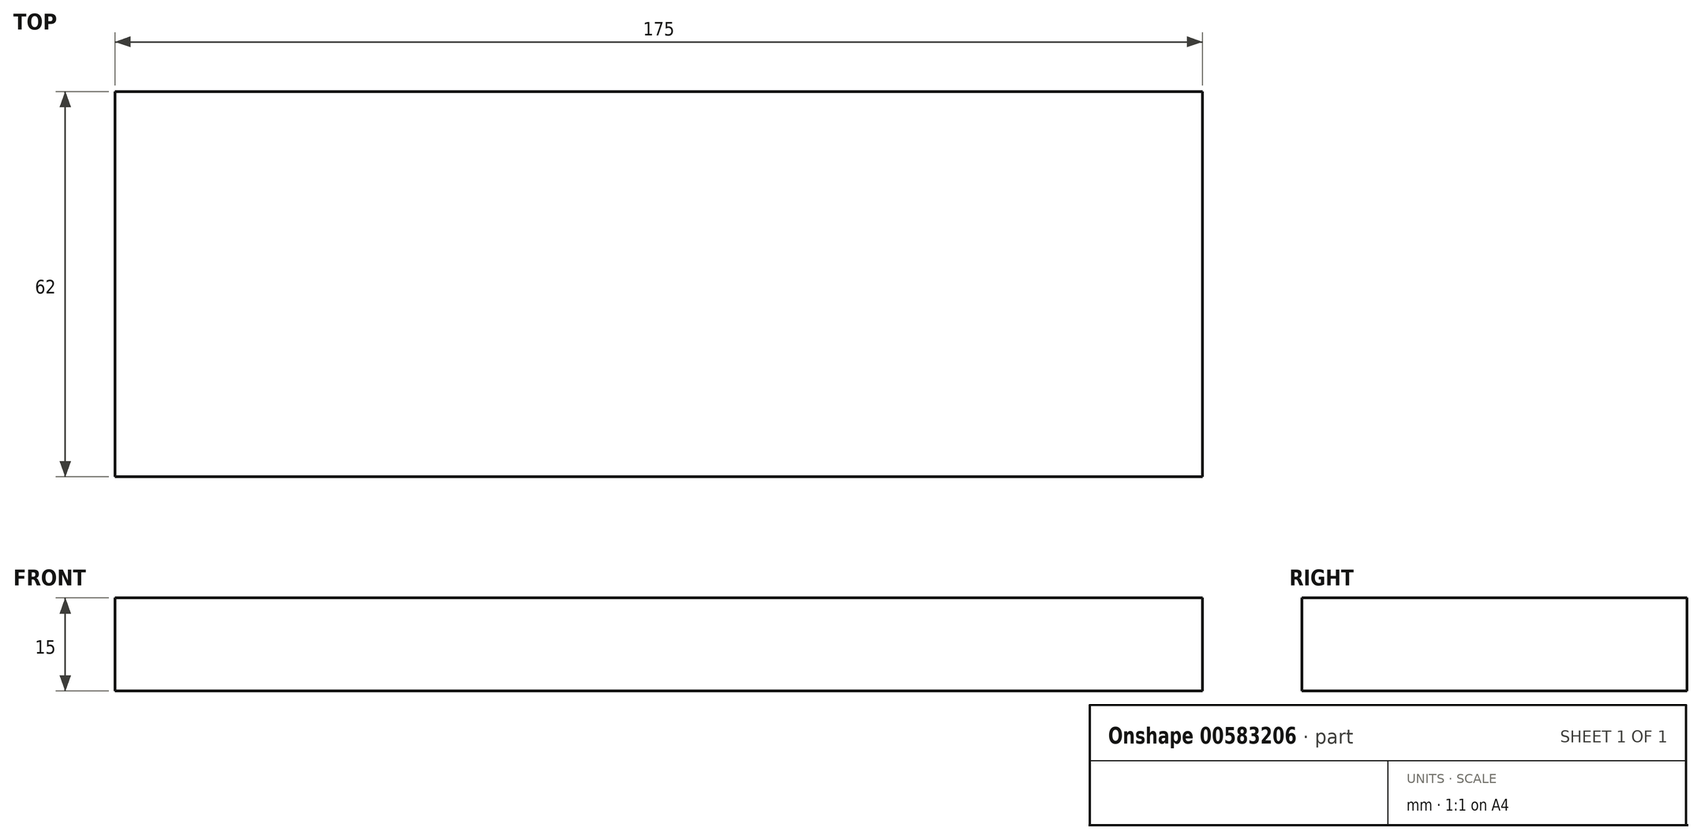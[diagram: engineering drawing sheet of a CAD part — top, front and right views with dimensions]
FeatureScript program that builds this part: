
annotation { "Feature Type Name" : "Feature", "Feature Type Description" : "" }
export const myFeature = defineFeature(function(context is Context, id is Id, definition is map)
    precondition{}
    {
        {
            var Q0;
            Q0=qCreatedBy(makeId("Front.planeOp"),FACE);
            var sketch = newSketch(context, id + "F0", { "sketchPlane" : qUnion([Q0])});
            skLineSegment(sketch, "E0", {"start": v(-93.41, -23.77) * mm, "end": v(81.59, -23.77) * mm});
            skLineSegment(sketch, "E1", {"start": v(81.59, -23.77) * mm, "end": v(81.59, -38.77) * mm});
            skLineSegment(sketch, "E2", {"start": v(81.59, -38.77) * mm, "end": v(-93.41, -38.77) * mm});
            skLineSegment(sketch, "E3", {"start": v(-93.41, -38.77) * mm, "end": v(-93.41, -23.77) * mm});
            skSolve(sketch);
        }
        {
            var Q0;
            Q0=makeQuery(id+"F0.imprint","IMPRINT",FACE,{"disambiguationData":[TD([[makeQuery(id+"F0.imprint","IMPRINT",EDGE,{"derivedFrom":sQuery(id+"F0.wireOp",EDGE,"E0")}),-1.0]])]});
            extrude(context, id + "F1", {"entities" : qUnion([Q0]), "depth" : 62 * mm, "offsetDistance" : 25 * mm});
        }
    });
